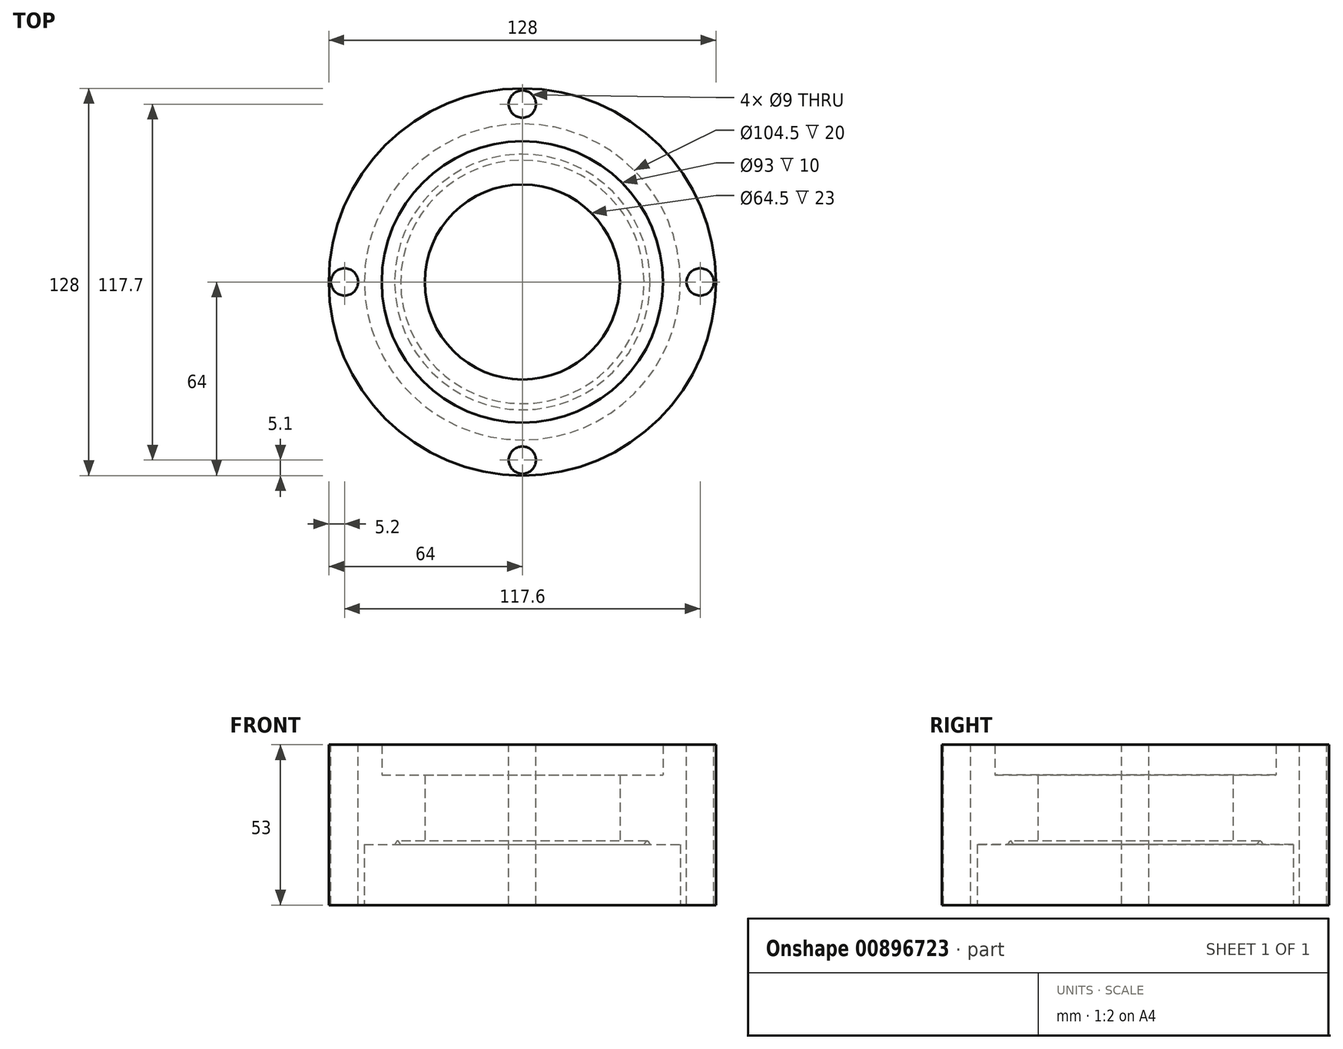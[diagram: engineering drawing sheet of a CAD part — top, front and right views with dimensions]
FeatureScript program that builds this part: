
annotation { "Feature Type Name" : "Feature", "Feature Type Description" : "" }
export const myFeature = defineFeature(function(context is Context, id is Id, definition is map)
    precondition{}
    {
        {
            var Q0;
            Q0=qCreatedBy(makeId("Front.planeOp"),FACE);
            var sketch = newSketch(context, id + "F0", { "sketchPlane" : qUnion([Q0])});
            skLineSegment(sketch, "E0", {"start": v(64, 0) * mm, "end": v(64, 53) * mm});
            skLineSegment(sketch, "E1", {"start": v(64, 53) * mm, "end": v(46.5, 53) * mm});
            skLineSegment(sketch, "E2", {"start": v(46.5, 53) * mm, "end": v(46.5, 43) * mm});
            skLineSegment(sketch, "E3", {"start": v(32.25, 43) * mm, "end": v(46.5, 43) * mm});
            skLineSegment(sketch, "E4", {"start": v(32.25, 43) * mm, "end": v(32.25, 20) * mm});
            skLineSegment(sketch, "E5", {"start": v(52.25, 0) * mm, "end": v(52.25, 20) * mm});
            skLineSegment(sketch, "E6", {"start": v(52.25, 20) * mm, "end": v(42.25, 20) * mm});
            skPoint(sketch, "E6.endSnap0", {"position": v(32.25, 21.5) * mm});
            skPoint(sketch, "E7.orphan", {"position": v(32.25, 0) * mm});
            skLineSegment(sketch, "E8.trimOffspring", {"start": v(52.25, 0) * mm, "end": v(64, 0) * mm});
            skPoint(sketch, "E9.start.orphan", {"position": v(0, 43) * mm});
            skLineSegment(sketch, "E10", {"start": v(0, 0) * mm, "end": v(0, 53) * mm});
            skLineSegment(sketch, "E11.trimOffspring", {"start": v(40.25, 20) * mm, "end": v(32.25, 20) * mm});
            skLineSegment(sketch, "E12", {"start": v(41.58, 21) * mm, "end": v(42.25, 20) * mm});
            skLineSegment(sketch, "E13", {"start": v(40.25, 20) * mm, "end": v(40.92, 21) * mm});
            skPoint(sketch, "E14.visualSharp", {"position": v(41.25, 21.5) * mm});
            skArc(sketch, "E14.filletArc", {"start": v(41.58, 21) * mm, "mid": v(41.25, 21.18) * mm, "end": v(40.92, 21) * mm});
            skSolve(sketch);
        }
        {
            var Q0;
            Q0=makeQuery(id+"F0.imprint","IMPRINT",FACE,{"disambiguationData":[TD([[makeQuery(id+"F0.imprint","IMPRINT",EDGE,{"derivedFrom":sQuery(id+"F0.wireOp",EDGE,"E0")}),1.0]])]});
            var Q1;
            Q1=sQuery(id+"F0.wireOp",EDGE,"E10");
            revolve(context, id + "F1", {"surfaceOperationType" : NewSurfaceOperationType.NEW, "entities" : qUnion([Q0]), "axis" : qUnion([Q1]), "revolveType" : RevolveType.FULL});
        }
        {
            var Q0;
            Q0=makeQuery(id+"F1.opRevolve","SWEPT_FACE",FACE,{"disambiguationData":[OSD([sQuery(id+"F0.wireOp",EDGE,"E1")])]});
            var sketch = newSketch(context, id + "F2", { "sketchPlane" : qUnion([Q0])});
            skCircle(sketch, "E15", {"center": v(0, 58.8) * mm, "radius": 4.5 * mm});
            skCircle(sketch, "E16", {"center": v(58.8, 0) * mm, "radius": 4.5 * mm});
            skCircle(sketch, "E17", {"center": v(0, -58.9) * mm, "radius": 4.5 * mm});
            skCircle(sketch, "E18", {"center": v(-58.8, 0) * mm, "radius": 4.5 * mm});
            skSolve(sketch);
        }
        {
            var Q0;
            Q0 = qSketchRegion(id + "F2", true);
            extrude(context, id + "F3", {"entities" : qUnion([Q0]), "operationType" : NewBodyOperationType.REMOVE, "oppositeDirection" : true, "depth" : 53 * mm, "offsetDistance" : 25 * mm});
        }
    });
